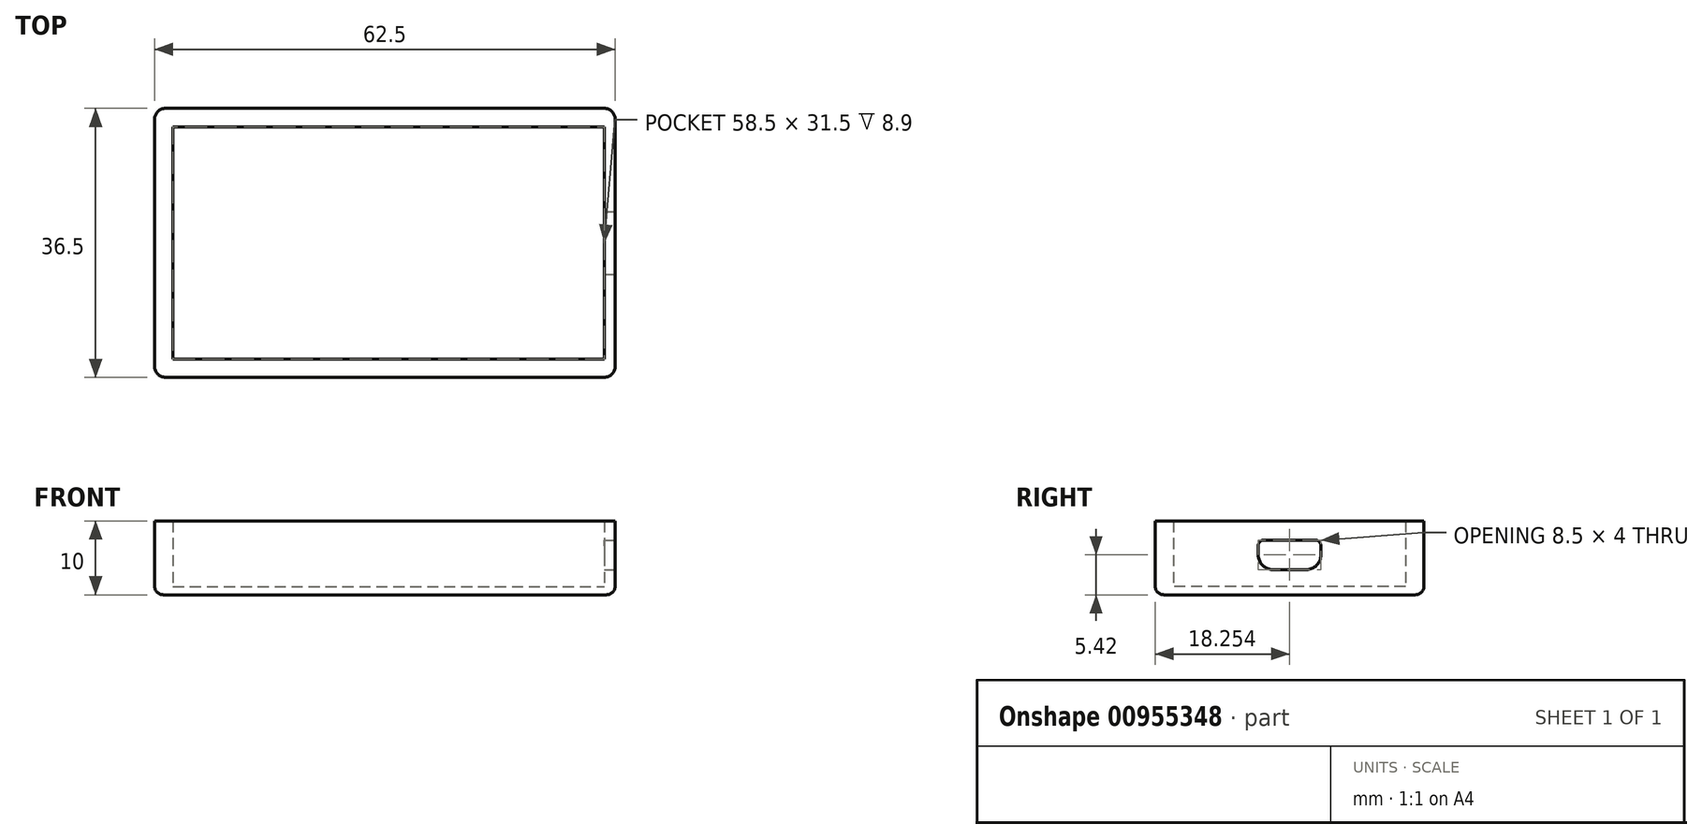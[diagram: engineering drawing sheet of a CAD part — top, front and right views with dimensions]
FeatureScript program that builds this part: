
annotation { "Feature Type Name" : "Feature", "Feature Type Description" : "" }
export const myFeature = defineFeature(function(context is Context, id is Id, definition is map)
    precondition{}
    {
        {
            var Q0;
            Q0=qCreatedBy(makeId("Top.planeOp"),FACE);
            var sketch = newSketch(context, id + "F0", { "sketchPlane" : qUnion([Q0])});
            skLineSegment(sketch, "E0.bottom", {"start": v(-31.24, 18.63) * mm, "end": v(31.26, 18.63) * mm});
            skLineSegment(sketch, "E0.top", {"start": v(-31.24, -17.87) * mm, "end": v(31.26, -17.87) * mm});
            skLineSegment(sketch, "E0.left", {"start": v(-31.24, 18.63) * mm, "end": v(-31.24, -17.87) * mm});
            skLineSegment(sketch, "E0.right", {"start": v(31.26, 18.63) * mm, "end": v(31.26, -17.87) * mm});
            skLineSegment(sketch, "E1.bottom", {"start": v(-28.74, 16.13) * mm, "end": v(29.76, 16.13) * mm});
            skLineSegment(sketch, "E1.top", {"start": v(-28.74, -15.37) * mm, "end": v(29.76, -15.37) * mm});
            skLineSegment(sketch, "E1.left", {"start": v(-28.74, 16.13) * mm, "end": v(-28.74, -15.37) * mm});
            skLineSegment(sketch, "E1.right", {"start": v(29.76, 16.13) * mm, "end": v(29.76, -15.37) * mm});
            skSolve(sketch);
        }
        {
            var Q0;
            Q0=makeQuery(id+"F0.imprint","IMPRINT",FACE,{"disambiguationData":[TD([[makeQuery(id+"F0.imprint","IMPRINT",EDGE,{"derivedFrom":sQuery(id+"F0.wireOp",EDGE,"E0.bottom")}),-1.0]])]});
            extrude(context, id + "F1", {"entities" : qUnion([Q0]), "depth" : 10 * mm, "offsetDistance" : 25.4 * mm});
        }
        {
            var Q0;
            Q0=makeQuery(id+"F0.imprint","IMPRINT",FACE,{"disambiguationData":[TD([[makeQuery(id+"F0.imprint","IMPRINT",EDGE,{"derivedFrom":sQuery(id+"F0.wireOp",EDGE,"E1.bottom")}),-1.0]])]});
            extrude(context, id + "F2", {"entities" : qUnion([Q0]), "operationType" : NewBodyOperationType.ADD, "depth" : 1.1 * mm, "offsetDistance" : 25 * mm});
        }
        {
            var Q0;
            Q0=makeQuery(id+"F1.opExtrude","SWEPT_EDGE",EDGE,{"disambiguationData":[OSD([sQuery(id+"F0.wireOp",EDGE,"E0.top"),sQuery(id+"F0.wireOp",EDGE,"E0.right")])]});
            var Q1;
            Q1=makeQuery(id+"F1.opExtrude","SWEPT_EDGE",EDGE,{"disambiguationData":[OSD([sQuery(id+"F0.wireOp",EDGE,"E0.bottom"),sQuery(id+"F0.wireOp",EDGE,"E0.right")])]});
            var Q2;
            Q2=makeQuery(id+"F1.opExtrude","SWEPT_EDGE",EDGE,{"disambiguationData":[OSD([sQuery(id+"F0.wireOp",EDGE,"E0.bottom"),sQuery(id+"F0.wireOp",EDGE,"E0.left")])]});
            var Q3;
            Q3=makeQuery(id+"F1.opExtrude","SWEPT_EDGE",EDGE,{"disambiguationData":[OSD([sQuery(id+"F0.wireOp",EDGE,"E0.top"),sQuery(id+"F0.wireOp",EDGE,"E0.left")])]});
            fillet(context, id + "F3", {"entities" : qUnion([Q0, Q1, Q2, Q3]), "radius" : 1.5 * mm, "tangentPropagation" : true, "allowEdgeOverflow" : false});
        }
        {
            var Q0;
            {var subQ0=sQuery(id+"F0.wireOp",EDGE,"E1.right");var subQ1=sQuery(id+"F0.wireOp",EDGE,"E1.left");var subQ2=sQuery(id+"F0.wireOp",EDGE,"E1.top");var subQ3=sQuery(id+"F0.wireOp",EDGE,"E1.bottom");Q0=makeQuery(id+"F2.boolean.opBoolean","MERGE",FACE,{"derivedFrom":[makeQuery(id+"F1.opExtrude","CAP_FACE",FACE,{"disambiguationData":[OSD([sQuery(id+"F0.wireOp",EDGE,"E0.bottom"),sQuery(id+"F0.wireOp",EDGE,"E0.top"),sQuery(id+"F0.wireOp",EDGE,"E0.left"),sQuery(id+"F0.wireOp",EDGE,"E0.right"),subQ3,subQ2,subQ1,subQ0])],"isStart":true}),makeQuery(id+"F2.opExtrude","CAP_FACE",FACE,{"disambiguationData":[OSD([subQ3,subQ2,subQ1,subQ0])],"isStart":true})]});}
            fillet(context, id + "F4", {"entities" : qUnion([Q0]), "radius" : 1.2 * mm, "tangentPropagation" : true, "allowEdgeOverflow" : false});
        }
        {
            var Q0;
            Q0=makeQuery(id+"F1.opExtrude","SWEPT_FACE",FACE,{"disambiguationData":[OSD([sQuery(id+"F0.wireOp",EDGE,"E0.right")])]});
            var sketch = newSketch(context, id + "F5", { "sketchPlane" : qUnion([Q0])});
            skLineSegment(sketch, "E2.bottom", {"start": v(-3.12, 7.42) * mm, "end": v(3.88, 7.42) * mm});
            skLineSegment(sketch, "E2.top", {"start": v(-1.87, 3.42) * mm, "end": v(2.63, 3.42) * mm});
            skLineSegment(sketch, "E2.left", {"start": v(-3.87, 6.67) * mm, "end": v(-3.87, 5.42) * mm});
            skLineSegment(sketch, "E2.right", {"start": v(4.63, 6.67) * mm, "end": v(4.63, 5.42) * mm});
            skPoint(sketch, "E3.visualSharp", {"position": v(-3.87, 3.42) * mm});
            skArc(sketch, "E3.filletArc", {"start": v(-3.87, 5.42) * mm, "mid": v(-3.28, 4) * mm, "end": v(-1.87, 3.42) * mm});
            skPoint(sketch, "E4.visualSharp", {"position": v(4.63, 3.42) * mm});
            skArc(sketch, "E4.filletArc", {"start": v(2.63, 3.42) * mm, "mid": v(4.05, 4) * mm, "end": v(4.63, 5.42) * mm});
            skPoint(sketch, "E5.visualSharp", {"position": v(4.63, 7.42) * mm});
            skArc(sketch, "E5.filletArc", {"start": v(4.63, 6.67) * mm, "mid": v(4.41, 7.2) * mm, "end": v(3.88, 7.42) * mm});
            skPoint(sketch, "E6.visualSharp", {"position": v(-3.87, 7.42) * mm});
            skArc(sketch, "E6.filletArc", {"start": v(-3.12, 7.42) * mm, "mid": v(-3.65, 7.2) * mm, "end": v(-3.87, 6.67) * mm});
            skSolve(sketch);
        }
        {
            var Q0;
            Q0=makeQuery(id+"F5.imprint","IMPRINT",FACE,{"disambiguationData":[TD([[makeQuery(id+"F5.imprint","IMPRINT",EDGE,{"derivedFrom":sQuery(id+"F5.wireOp",EDGE,"E2.bottom")}),-1.0]])]});
            extrude(context, id + "F6", {"entities" : qUnion([Q0]), "operationType" : NewBodyOperationType.REMOVE, "oppositeDirection" : true, "depth" : 3 * mm, "offsetDistance" : 25 * mm});
        }
    });
